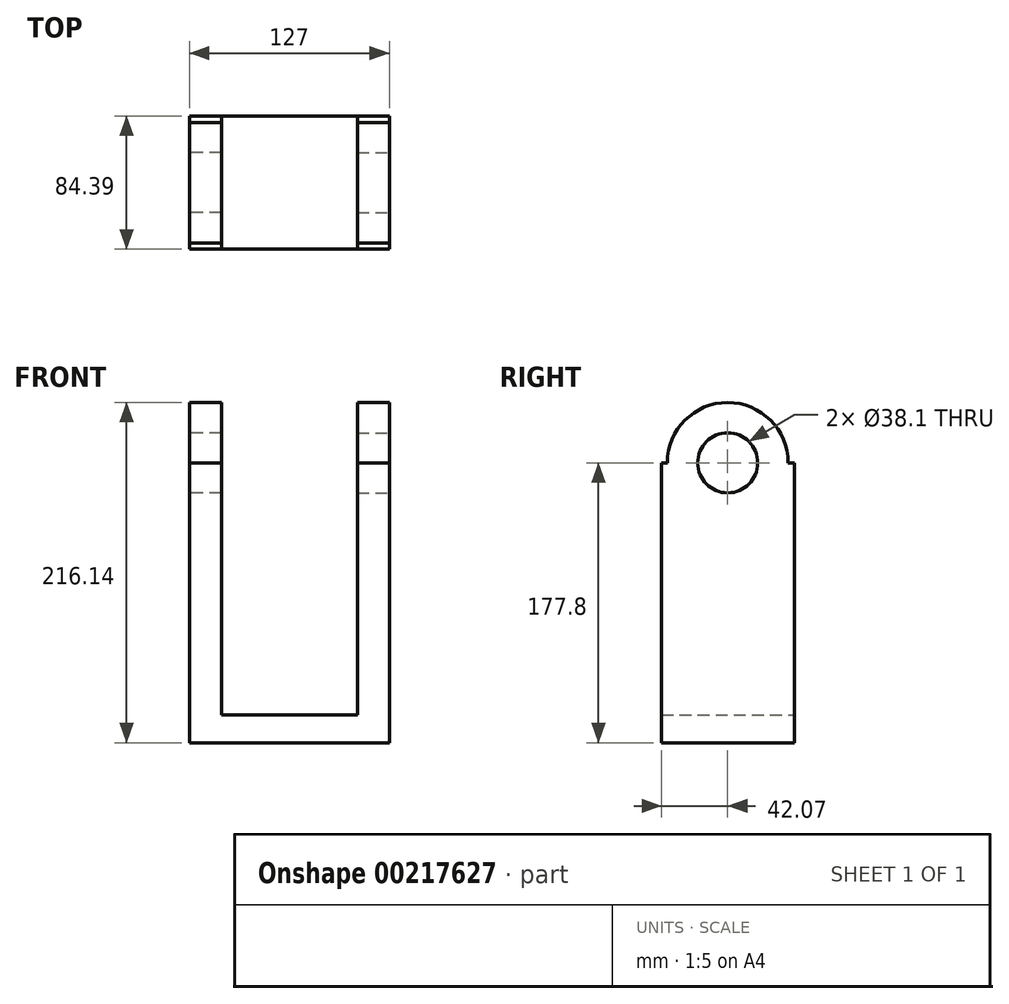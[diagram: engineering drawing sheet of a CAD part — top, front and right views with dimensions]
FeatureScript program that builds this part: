
annotation { "Feature Type Name" : "Feature", "Feature Type Description" : "" }
export const myFeature = defineFeature(function(context is Context, id is Id, definition is map)
    precondition{}
    {
        {
            var Q0;
            Q0=qCreatedBy(makeId("Right.planeOp"),FACE);
            var sketch = newSketch(context, id + "F0", { "sketchPlane" : qUnion([Q0])});
            skCircle(sketch, "E0", {"center": v(0, 0) * mm, "radius": 19.05 * mm});
            skLineSegment(sketch, "E1.bottom", {"start": v(-42.07, 0) * mm, "end": v(-38.34, 0) * mm});
            skLineSegment(sketch, "E1.top", {"start": v(-42.07, -177.8) * mm, "end": v(42.32, -177.8) * mm});
            skLineSegment(sketch, "E1.left", {"start": v(-42.07, 0) * mm, "end": v(-42.07, -177.8) * mm});
            skLineSegment(sketch, "E1.right", {"start": v(42.32, 0) * mm, "end": v(42.32, -177.8) * mm});
            skArc(sketch, "E2", {"start": v(38.34, 0) * mm, "mid": v(0, 38.34) * mm, "end": v(-38.34, 0) * mm});
            skLineSegment(sketch, "E3.trimOffspring", {"start": v(38.34, 0) * mm, "end": v(42.32, 0) * mm});
            skSolve(sketch);
        }
        {
            var Q0;
            Q0=makeQuery(id+"F0.imprint","IMPRINT",FACE,{"disambiguationData":[TD([[makeQuery(id+"F0.imprint","IMPRINT",EDGE,{"derivedFrom":sQuery(id+"F0.wireOp",EDGE,"E0")}),-1.0]])]});
            extrude(context, id + "F1", {"entities" : qUnion([Q0]), "depth" : 20.32 * mm});
        }
        {
            var Q0;
            Q0=makeQuery(id+"F1.opExtrude","CAP_FACE",FACE,{"disambiguationData":[OSD([sQuery(id+"F0.wireOp",EDGE,"E0"),sQuery(id+"F0.wireOp",EDGE,"E1.bottom"),sQuery(id+"F0.wireOp",EDGE,"E1.top"),sQuery(id+"F0.wireOp",EDGE,"E1.left"),sQuery(id+"F0.wireOp",EDGE,"E1.right"),sQuery(id+"F0.wireOp",EDGE,"E2"),sQuery(id+"F0.wireOp",EDGE,"E3.trimOffspring")])],"isStart":false});
            var sketch = newSketch(context, id + "F2", { "sketchPlane" : qUnion([Q0])});
            skLineSegment(sketch, "E4.bottom", {"start": v(-42.07, -177.8) * mm, "end": v(42.32, -177.8) * mm});
            skLineSegment(sketch, "E4.top", {"start": v(-42.07, -160.06) * mm, "end": v(42.32, -160.06) * mm});
            skLineSegment(sketch, "E4.left", {"start": v(-42.07, -177.8) * mm, "end": v(-42.07, -160.06) * mm});
            skLineSegment(sketch, "E4.right", {"start": v(42.32, -177.8) * mm, "end": v(42.32, -160.06) * mm});
            skSolve(sketch);
        }
        {
            var Q0;
            Q0=makeQuery(id+"F2.imprint","IMPRINT",FACE,{"disambiguationData":[TD([[makeQuery(id+"F2.imprint","IMPRINT",EDGE,{"derivedFrom":sQuery(id+"F2.wireOp",EDGE,"E4.bottom")}),1.0]])]});
            extrude(context, id + "F3", {"entities" : qUnion([Q0]), "operationType" : NewBodyOperationType.ADD, "depth" : 43.18 * mm});
        }
        {
            var Q0;
            Q0=makeQuery(id+"F1.opExtrude","SWEPT_BODY",BODY,{"disambiguationData":[OSD([sQuery(id+"F0.wireOp",EDGE,"E0"),sQuery(id+"F0.wireOp",EDGE,"E1.bottom"),sQuery(id+"F0.wireOp",EDGE,"E1.top"),sQuery(id+"F0.wireOp",EDGE,"E1.left"),sQuery(id+"F0.wireOp",EDGE,"E1.right"),sQuery(id+"F0.wireOp",EDGE,"E2"),sQuery(id+"F0.wireOp",EDGE,"E3.trimOffspring")])]});
            var Q1;
            Q1=makeQuery(id+"F3.opExtrude","CAP_FACE",FACE,{"disambiguationData":[OSD([sQuery(id+"F2.wireOp",EDGE,"E4.bottom"),sQuery(id+"F2.wireOp",EDGE,"E4.top"),sQuery(id+"F2.wireOp",EDGE,"E4.left"),sQuery(id+"F2.wireOp",EDGE,"E4.right")])],"isStart":false});
            mirror(context, id + "F4", {"operationType" : NewBodyOperationType.ADD, "entities" : qUnion([Q0]), "mirrorPlane" : qUnion([Q1])});
        }
    });
